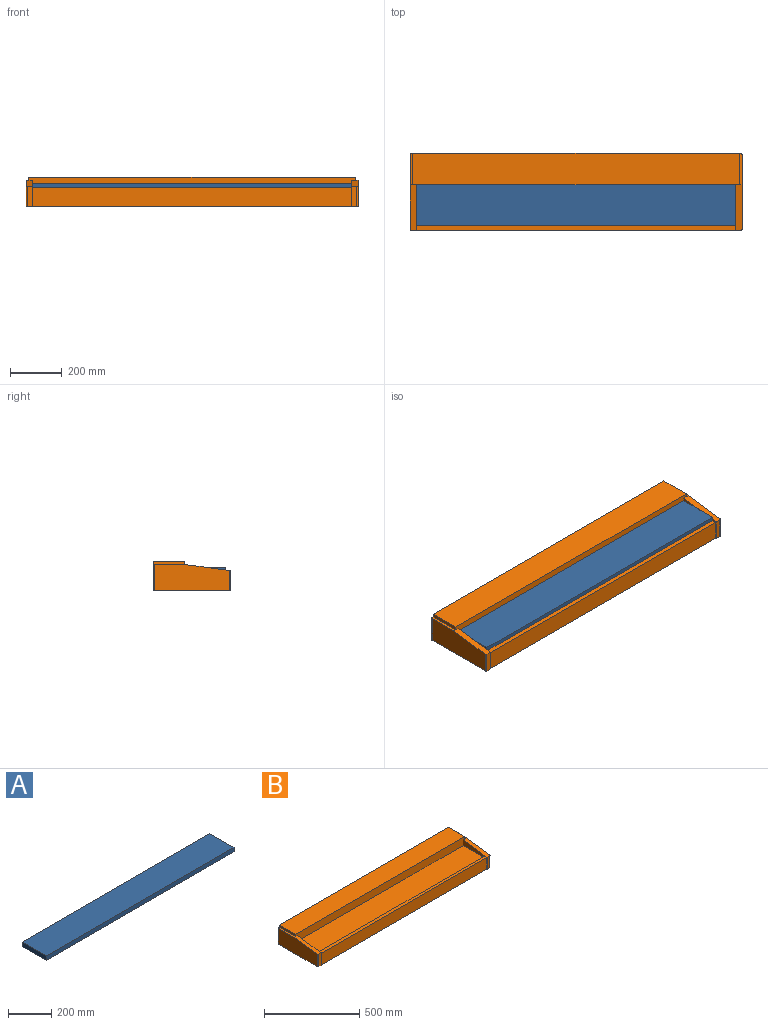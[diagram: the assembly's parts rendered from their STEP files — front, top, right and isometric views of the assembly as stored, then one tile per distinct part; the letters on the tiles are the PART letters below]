
ASSEMBLY  parts=2 mates=1
PART A: 6 faces, bbox 1233x158x25 mm
  f0: plane 1233x25mm, normal (0,1,0), area 30825mm2, adj f1,f3,f4,f5
  f1: plane 158x25mm, normal (-1,0,0), area 3950mm2, adj f0,f2,f4,f5
  f2: plane 1233x25mm, normal (0,-1,0), area 30825mm2, adj f1,f3,f4,f5
  f3: plane 158x25mm, normal (1,0,0), area 3950mm2, adj f0,f2,f4,f5
  f4: plane 1233x158mm, normal (0,0,-1), area 194814mm2, adj f0,f1,f2,f3
  f5: plane 1233x158mm, normal (0,0,1), area 194814mm2, adj f0,f1,f2,f3
PART B: 26 faces, bbox 1283x300x115 mm
  f0: plane 77.99x20mm, normal (0,-1,0), area 1559.9mm2, adj f13,f15,f18,f22
  f1: plane 1233x18mm, normal (0,0,1), area 22194mm2, adj f5,f13,f19,f21
  f2: plane 122x25mm, normal (0,0,1), area 1336.6mm2, adj f4,f5,f8,f9,f10,f17,f24
  f3: plane 78.05x20mm, normal (0,-1,0), area 1561.1mm2, adj f5,f17,f18,f23
  f4: plane 290x102mm, normal (1,0,0), area 27566.8mm2, adj f2,f17,f18,f23,f24
  f5: plane 178x102mm, normal (-1,0,0), area 4404.8mm2, adj f1,f2,f3,f10,f17,f18,f19,f20
  f6: plane 1261x122mm, normal (0,0,1), area 153842mm2, adj f8,f9,f10,f11
  f7: plane 290x102mm, normal (-1,0,0), area 27561.6mm2, adj f12,f15,f18,f22,f25
  f8: plane 1273x115mm, normal (0,1,0), area 146239mm2, adj f2,f6,f9,f11,f12,f18,f24,f25
  f9: plane 122x13mm, normal (1,0,0), area 1586mm2, adj f2,f6,f8,f10
  f10: plane 1261x50mm, normal (0,-1,0), area 62014mm2, adj f2,f5,f6,f9,f11,f13,f14,f16
  f11: plane 122x13mm, normal (-1,0,0), area 1586mm2, adj f6,f8,f10,f12,f14
  f12: plane 121.98x11mm, normal (0,0,1), area 1336.4mm2, adj f7,f8,f11,f15,f25
  f13: plane 178x102mm, normal (1,0,0), area 4399.2mm2, adj f0,f1,f10,f15,f18,f19,f20,f21
  f14: plane 14x0.02mm, normal (0,0,-1), area 0.3mm2, adj f10,f11,f15,f16
  f15: plane 178.02x25mm, normal (0,-0.13,0.99), area 4485.4mm2, adj f0,f7,f12,f13,f14,f16,f22
  f16: plane 0.02x0mm, normal (-1,0,0), area 0mm2, adj f10,f14,f15
  f17: plane 178x25mm, normal (0,-0.13,0.99), area 4484.7mm2, adj f2,f3,f4,f5,f23
  f18: plane 1283x300mm, normal (0,0,-1), area 382412.5mm2, adj f0,f3,f4,f5,f7,f8,f13,f21
  f19: plane 1233x10mm, normal (0,1,0), area 12330mm2, adj f1,f5,f13,f20
  f20: plane 1233x158mm, normal (0,0,1), area 194814mm2, adj f5,f10,f13,f19
  f21: plane 1233x75mm, normal (0,-1,0), area 92475mm2, adj f1,f5,f13,f18
  f22: cylinder r=5mm len=78.67mm, axis (0,0,1), area 614.5mm2, adj f0,f7,f15,f18
  f23: cylinder r=5mm len=78.73mm, axis (0,0,-1), area 614.9mm2, adj f3,f4,f17,f18
  f24: cylinder r=5mm len=102mm, axis (0,0,1), area 801.1mm2, adj f2,f4,f8,f18
  f25: cylinder r=5mm len=102mm, axis (0,0,-1), area 801.1mm2, adj f7,f8,f12,f18
PLACE A at identity
PLACE B at identity
MATE fastened A.f4 <-> B.f20  axis (0,0,-1) through (13.63,164.58,65)mm
